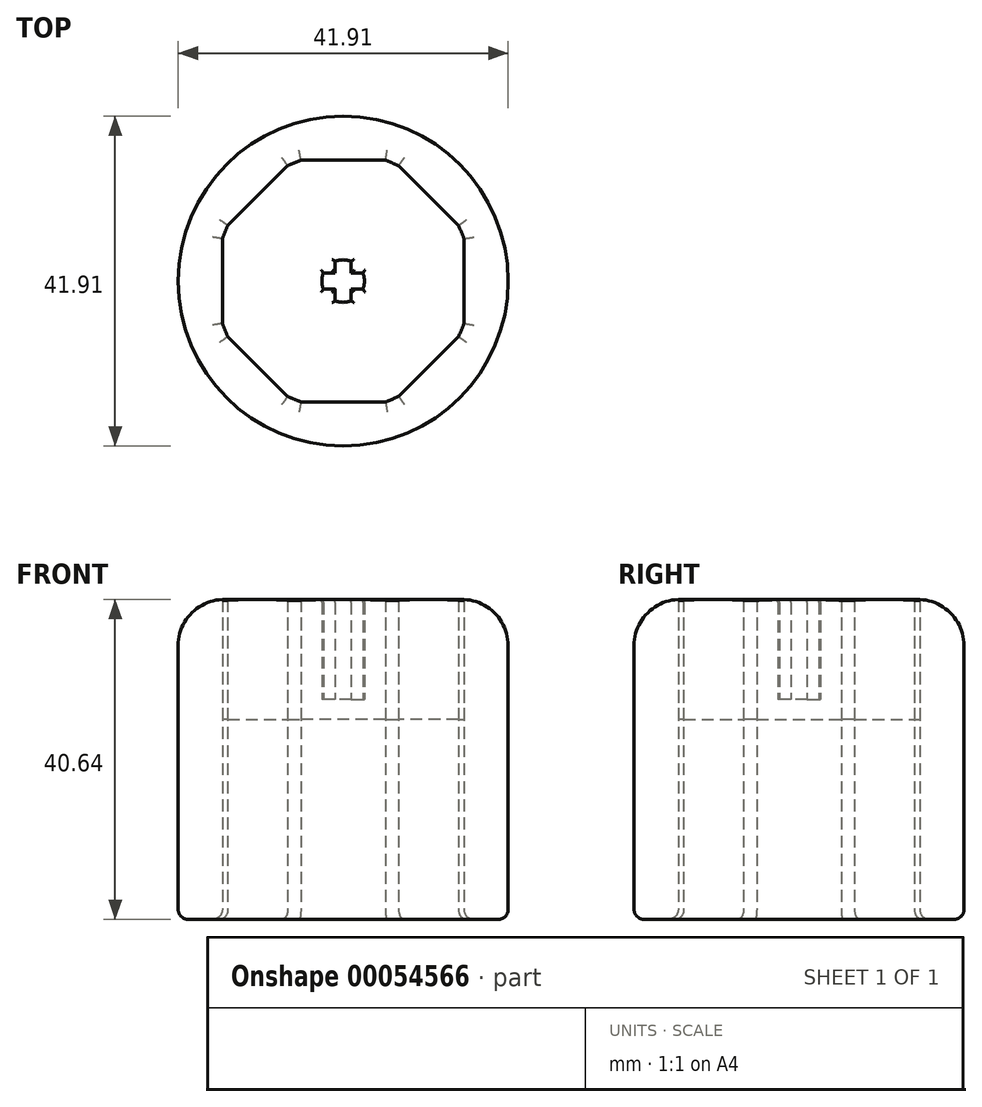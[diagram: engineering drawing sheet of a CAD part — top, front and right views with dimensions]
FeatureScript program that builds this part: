
annotation { "Feature Type Name" : "Feature", "Feature Type Description" : "" }
export const myFeature = defineFeature(function(context is Context, id is Id, definition is map)
    precondition{}
    {
        {
            var Q0;
            Q0=qCreatedBy(makeId("Top.planeOp"),FACE);
            var sketch = newSketch(context, id + "F0", { "sketchPlane" : qUnion([Q0])});
            skLineSegment(sketch, "E0.6.0", {"start": v(-22.54, 38.16) * mm, "end": v(-22.54, 27.4) * mm});
            skLineSegment(sketch, "E0.4.0", {"start": v(-32.51, 17.44) * mm, "end": v(-43.26, 17.44) * mm});
            skLineSegment(sketch, "E0.3.0", {"start": v(-44.93, 18.13) * mm, "end": v(-52.54, 25.73) * mm});
            skLineSegment(sketch, "E0.7.0", {"start": v(-30.84, 47.43) * mm, "end": v(-23.24, 39.83) * mm});
            skLineSegment(sketch, "E0.5.0", {"start": v(-23.24, 25.73) * mm, "end": v(-30.84, 18.13) * mm});
            skLineSegment(sketch, "E0.2.0", {"start": v(-53.23, 27.4) * mm, "end": v(-53.23, 38.16) * mm});
            skLineSegment(sketch, "E0.1.0", {"start": v(-52.54, 39.83) * mm, "end": v(-44.93, 47.43) * mm});
            skLineSegment(sketch, "E1", {"start": v(-43.26, 48.12) * mm, "end": v(-32.51, 48.12) * mm});
            skArc(sketch, "E2.trimOffspring", {"start": v(-32.51, 17.44) * mm, "mid": v(-31.67, 17.76) * mm, "end": v(-30.84, 18.13) * mm});
            skArc(sketch, "E3.trimOffspring", {"start": v(-30.84, 47.43) * mm, "mid": v(-31.67, 47.8) * mm, "end": v(-32.51, 48.12) * mm});
            skArc(sketch, "E4.trimOffspring", {"start": v(-43.26, 48.12) * mm, "mid": v(-44.1, 47.8) * mm, "end": v(-44.93, 47.43) * mm});
            skArc(sketch, "E5", {"start": v(-52.54, 39.83) * mm, "mid": v(-52.9, 39) * mm, "end": v(-53.23, 38.16) * mm});
            skArc(sketch, "E6.trimOffspring", {"start": v(-22.54, 38.16) * mm, "mid": v(-22.87, 39) * mm, "end": v(-23.24, 39.83) * mm});
            skArc(sketch, "E7.trimOffspring", {"start": v(-53.23, 27.4) * mm, "mid": v(-52.9, 26.56) * mm, "end": v(-52.54, 25.73) * mm});
            skArc(sketch, "E8.trimOffspring", {"start": v(-44.93, 18.13) * mm, "mid": v(-44.1, 17.76) * mm, "end": v(-43.26, 17.44) * mm});
            skArc(sketch, "E9.trimOffspring", {"start": v(-23.24, 25.73) * mm, "mid": v(-22.87, 26.56) * mm, "end": v(-22.54, 27.4) * mm});
            skCircle(sketch, "E10", {"center": v(-37.89, 32.78) * mm, "radius": 20.96 * mm});
            skLineSegment(sketch, "E11", {"start": v(-38.9, 31.77) * mm, "end": v(-38.9, 30.28) * mm});
            skLineSegment(sketch, "E12", {"start": v(-36.87, 31.77) * mm, "end": v(-35.38, 31.77) * mm});
            skLineSegment(sketch, "E13", {"start": v(-36.87, 33.8) * mm, "end": v(-36.87, 35.28) * mm});
            skLineSegment(sketch, "E14", {"start": v(-38.9, 31.77) * mm, "end": v(-40.39, 31.77) * mm});
            skArc(sketch, "E15.trimOffspring", {"start": v(-35.38, 31.77) * mm, "mid": v(-35.19, 32.78) * mm, "end": v(-35.38, 33.8) * mm});
            skLineSegment(sketch, "E16", {"start": v(-38.9, 33.8) * mm, "end": v(-40.39, 33.8) * mm});
            skArc(sketch, "E17.trimOffspring", {"start": v(-40.39, 33.8) * mm, "mid": v(-40.59, 32.78) * mm, "end": v(-40.39, 31.77) * mm});
            skLineSegment(sketch, "E18", {"start": v(-38.9, 33.8) * mm, "end": v(-38.9, 35.28) * mm});
            skLineSegment(sketch, "E19", {"start": v(-36.87, 31.77) * mm, "end": v(-36.87, 30.28) * mm});
            skArc(sketch, "E20.trimOffspring", {"start": v(-38.9, 30.28) * mm, "mid": v(-37.89, 30.08) * mm, "end": v(-36.87, 30.28) * mm});
            skArc(sketch, "E21", {"start": v(-36.87, 35.28) * mm, "mid": v(-37.89, 35.48) * mm, "end": v(-38.9, 35.28) * mm});
            skLineSegment(sketch, "E22", {"start": v(-36.87, 33.8) * mm, "end": v(-35.38, 33.8) * mm});
            skCircle(sketch, "E23", {"center": v(-37.89, 32.78) * mm, "radius": 6.35 * mm});
            skSolve(sketch);
        }
        {
            var Q0;
            Q0=makeQuery(id+"F0.imprint","IMPRINT",FACE,{"disambiguationData":[TD([[makeQuery(id+"F0.imprint","IMPRINT",EDGE,{"derivedFrom":sQuery(id+"F0.wireOp",EDGE,"E11")}),1.0]])]});
            extrude(context, id + "F1", {"entities" : qUnion([Q0]), "depth" : 27.94 * mm, "hasSecondDirection" : true, "secondDirectionOppositeDirection" : false, "secondDirectionDepth" : 25.4 * mm});
        }
        {
            var Q0;
            Q0=makeQuery(id+"F0.imprint","IMPRINT",FACE,{"disambiguationData":[TD([[makeQuery(id+"F0.imprint","IMPRINT",EDGE,{"derivedFrom":sQuery(id+"F0.wireOp",EDGE,"E11")}),-1.0]])]});
            extrude(context, id + "F2", {"entities" : qUnion([Q0]), "operationType" : NewBodyOperationType.ADD, "depth" : 40.64 * mm, "hasSecondDirection" : true, "secondDirectionOppositeDirection" : false, "secondDirectionDepth" : 25.4 * mm});
        }
        {
            var Q0;
            Q0=makeQuery(id+"F0.imprint","IMPRINT",FACE,{"disambiguationData":[TD([[makeQuery(id+"F0.imprint","IMPRINT",EDGE,{"derivedFrom":sQuery(id+"F0.wireOp",EDGE,"E0.6.0")}),-1.0]])]});
            extrude(context, id + "F3", {"entities" : qUnion([Q0]), "operationType" : NewBodyOperationType.ADD, "depth" : 40.64 * mm, "hasSecondDirection" : true, "secondDirectionOppositeDirection" : false, "secondDirectionDepth" : 25.4 * mm});
        }
        {
            var Q0;
            Q0=makeQuery(id+"F0.imprint","IMPRINT",FACE,{"disambiguationData":[TD([[makeQuery(id+"F0.imprint","IMPRINT",EDGE,{"derivedFrom":sQuery(id+"F0.wireOp",EDGE,"E0.6.0")}),1.0]])]});
            extrude(context, id + "F4", {"entities" : qUnion([Q0]), "depth" : 40.64 * mm});
        }
        {
            var Q0;
            Q0=makeQuery(id+"F2.opExtrude","CAP_EDGE",EDGE,{"disambiguationData":[OSD([sQuery(id+"F0.wireOp",EDGE,"8cce3f25-2efd-4c49-95cc-eba16443d6be")])],"isStart":false});
            var Q1;
            Q1=makeQuery(id+"F2.opExtrude","CAP_EDGE",EDGE,{"disambiguationData":[OSD([sQuery(id+"F0.wireOp",EDGE,"d85cb93b-5381-4659-b75b-9c5bd339f56e.trimOffspring")])],"isStart":false});
            var Q2;
            Q2=makeQuery(id+"F2.opExtrude","CAP_EDGE",EDGE,{"disambiguationData":[OSD([sQuery(id+"F0.wireOp",EDGE,"1c712a26-7b62-46fb-a9db-95f78db6a6e8")])],"isStart":false});
            var Q3;
            Q3=makeQuery(id+"F2.opExtrude","CAP_EDGE",EDGE,{"disambiguationData":[OSD([sQuery(id+"F0.wireOp",EDGE,"b9b189e9-58f7-485b-9be6-83cfb21979a9")])],"isStart":false});
            var Q4;
            Q4=makeQuery(id+"F2.opExtrude","CAP_EDGE",EDGE,{"disambiguationData":[OSD([sQuery(id+"F0.wireOp",EDGE,"06b7407c-ebd2-401f-a168-bfd0f99af218.trimOffspring")])],"isStart":false});
            var Q5;
            Q5=makeQuery(id+"F2.opExtrude","CAP_EDGE",EDGE,{"disambiguationData":[OSD([sQuery(id+"F0.wireOp",EDGE,"24feb4b3-b69e-498d-8aa6-f2a153c40b04")])],"isStart":false});
            var Q6;
            Q6=makeQuery(id+"F2.opExtrude","CAP_EDGE",EDGE,{"disambiguationData":[OSD([sQuery(id+"F0.wireOp",EDGE,"b4d91fd9-bfef-4f18-a990-5c9c65c2c351.trimOffspring")])],"isStart":false});
            var Q7;
            Q7=makeQuery(id+"F2.opExtrude","CAP_EDGE",EDGE,{"disambiguationData":[OSD([sQuery(id+"F0.wireOp",EDGE,"6bb57907-a155-48d2-a021-7ef5ce16fcda")])],"isStart":false});
            var Q8;
            Q8=makeQuery(id+"F2.opExtrude","CAP_EDGE",EDGE,{"disambiguationData":[OSD([sQuery(id+"F0.wireOp",EDGE,"65d8ba4e-4099-4971-ac6f-0856e3ba22bd")])],"isStart":false});
            var Q9;
            Q9=makeQuery(id+"F2.opExtrude","CAP_EDGE",EDGE,{"disambiguationData":[OSD([sQuery(id+"F0.wireOp",EDGE,"1507f4e8-23c1-4ea5-b1ae-361abdb5c639")])],"isStart":false});
            var Q10;
            Q10=makeQuery(id+"F2.opExtrude","CAP_EDGE",EDGE,{"disambiguationData":[OSD([sQuery(id+"F0.wireOp",EDGE,"df5c5b97-d7ba-45ac-b841-1a60e982e43c")])],"isStart":false});
            var Q11;
            Q11=makeQuery(id+"F2.opExtrude","CAP_EDGE",EDGE,{"disambiguationData":[OSD([sQuery(id+"F0.wireOp",EDGE,"63e4fde5-60d5-43d3-8cb7-058ddb4870cb")])],"isStart":false});
            var Q12;
            Q12=makeQuery(id+"F2.opExtrude","CAP_EDGE",EDGE,{"disambiguationData":[OSD([sQuery(id+"F0.wireOp",EDGE,"E22")])],"isStart":false});
            var Q13;
            Q13=makeQuery(id+"F2.opExtrude","CAP_EDGE",EDGE,{"disambiguationData":[OSD([sQuery(id+"F0.wireOp",EDGE,"E15.trimOffspring")])],"isStart":false});
            var Q14;
            Q14=makeQuery(id+"F2.opExtrude","CAP_EDGE",EDGE,{"disambiguationData":[OSD([sQuery(id+"F0.wireOp",EDGE,"E19")])],"isStart":false});
            var Q15;
            Q15=makeQuery(id+"F2.opExtrude","CAP_EDGE",EDGE,{"disambiguationData":[OSD([sQuery(id+"F0.wireOp",EDGE,"E13")])],"isStart":false});
            var Q16;
            Q16=makeQuery(id+"F2.opExtrude","CAP_EDGE",EDGE,{"disambiguationData":[OSD([sQuery(id+"F0.wireOp",EDGE,"E21")])],"isStart":false});
            var Q17;
            Q17=makeQuery(id+"F2.opExtrude","CAP_EDGE",EDGE,{"disambiguationData":[OSD([sQuery(id+"F0.wireOp",EDGE,"E12")])],"isStart":false});
            var Q18;
            Q18=makeQuery(id+"F2.opExtrude","CAP_EDGE",EDGE,{"disambiguationData":[OSD([sQuery(id+"F0.wireOp",EDGE,"E16")])],"isStart":false});
            var Q19;
            Q19=makeQuery(id+"F2.opExtrude","CAP_EDGE",EDGE,{"disambiguationData":[OSD([sQuery(id+"F0.wireOp",EDGE,"E18")])],"isStart":false});
            var Q20;
            Q20=makeQuery(id+"F2.opExtrude","CAP_EDGE",EDGE,{"disambiguationData":[OSD([sQuery(id+"F0.wireOp",EDGE,"E14")])],"isStart":false});
            var Q21;
            Q21=makeQuery(id+"F2.opExtrude","CAP_EDGE",EDGE,{"disambiguationData":[OSD([sQuery(id+"F0.wireOp",EDGE,"E17.trimOffspring")])],"isStart":false});
            var Q22;
            Q22=makeQuery(id+"F2.opExtrude","CAP_EDGE",EDGE,{"disambiguationData":[OSD([sQuery(id+"F0.wireOp",EDGE,"E11")])],"isStart":false});
            var Q23;
            Q23=makeQuery(id+"F2.opExtrude","CAP_EDGE",EDGE,{"disambiguationData":[OSD([sQuery(id+"F0.wireOp",EDGE,"E20.trimOffspring")])],"isStart":false});
            fillet(context, id + "F5", {"entities" : qUnion([Q0, Q1, Q2, Q3, Q4, Q5, Q6, Q7, Q8, Q9, Q10, Q11, Q12, Q13, Q14, Q15, Q16, Q17, Q18, Q19, Q20, Q21, Q22, Q23]), "radius" : 0.38 * mm, "tangentPropagation" : true, "allowEdgeOverflow" : false});
        }
        {
            var Q0;
            Q0=makeQuery(id+"F4.opExtrude","CAP_EDGE",EDGE,{"disambiguationData":[OSD([sQuery(id+"F0.wireOp",EDGE,"34b97c57-4139-4ba9-9a9e-a1f90fe492f6")])],"isStart":false});
            var Q1;
            Q1=makeQuery(id+"F4.opExtrude","CAP_EDGE",EDGE,{"disambiguationData":[OSD([sQuery(id+"F0.wireOp",EDGE,"E10")])],"isStart":false});
            fillet(context, id + "F6", {"entities" : qUnion([Q0, Q1]), "radius" : 5.84 * mm, "tangentPropagation" : true, "allowEdgeOverflow" : false});
        }
        {
            var Q0;
            Q0=makeQuery(id+"F4.opExtrude","CAP_EDGE",EDGE,{"disambiguationData":[OSD([sQuery(id+"F0.wireOp",EDGE,"34b97c57-4139-4ba9-9a9e-a1f90fe492f6")])],"isStart":true});
            var Q1;
            Q1=makeQuery(id+"F4.opExtrude","CAP_EDGE",EDGE,{"disambiguationData":[OSD([sQuery(id+"F0.wireOp",EDGE,"e68f5cd1-f7fe-44bd-84ca-22998c78a58e.3.0")])],"isStart":true});
            var Q2;
            Q2=makeQuery(id+"F4.opExtrude","CAP_EDGE",EDGE,{"disambiguationData":[OSD([sQuery(id+"F0.wireOp",EDGE,"e68f5cd1-f7fe-44bd-84ca-22998c78a58e.2.0")])],"isStart":true});
            var Q3;
            Q3=makeQuery(id+"F4.opExtrude","CAP_EDGE",EDGE,{"disambiguationData":[OSD([sQuery(id+"F0.wireOp",EDGE,"19dd5a60-77d2-466b-ad95-392809fea93a.trimOffspring")])],"isStart":true});
            var Q4;
            Q4=makeQuery(id+"F4.opExtrude","CAP_EDGE",EDGE,{"disambiguationData":[OSD([sQuery(id+"F0.wireOp",EDGE,"cbcc1692-128e-4c7d-bcf3-f8956db3017d.trimOffspring")])],"isStart":true});
            var Q5;
            Q5=makeQuery(id+"F4.opExtrude","CAP_EDGE",EDGE,{"disambiguationData":[OSD([sQuery(id+"F0.wireOp",EDGE,"e68f5cd1-f7fe-44bd-84ca-22998c78a58e.4.0")])],"isStart":true});
            var Q6;
            Q6=makeQuery(id+"F4.opExtrude","CAP_EDGE",EDGE,{"disambiguationData":[OSD([sQuery(id+"F0.wireOp",EDGE,"9069cb0e-2177-4baf-a3e2-3174a85d6ad9.trimOffspring")])],"isStart":true});
            var Q7;
            Q7=makeQuery(id+"F4.opExtrude","CAP_EDGE",EDGE,{"disambiguationData":[OSD([sQuery(id+"F0.wireOp",EDGE,"e68f5cd1-f7fe-44bd-84ca-22998c78a58e.5.0")])],"isStart":true});
            var Q8;
            Q8=makeQuery(id+"F4.opExtrude","CAP_EDGE",EDGE,{"disambiguationData":[OSD([sQuery(id+"F0.wireOp",EDGE,"e68f5cd1-f7fe-44bd-84ca-22998c78a58e.1.0")])],"isStart":true});
            var Q9;
            Q9=makeQuery(id+"F4.opExtrude","CAP_EDGE",EDGE,{"disambiguationData":[OSD([sQuery(id+"F0.wireOp",EDGE,"f1c67b7e-82c5-4710-8c8e-e395814cc59c")])],"isStart":true});
            var Q10;
            Q10=makeQuery(id+"F4.opExtrude","CAP_EDGE",EDGE,{"disambiguationData":[OSD([sQuery(id+"F0.wireOp",EDGE,"e37a4532-e548-428b-b1e3-5847a7a48128.trimOffspring")])],"isStart":true});
            var Q11;
            Q11=makeQuery(id+"F4.opExtrude","CAP_EDGE",EDGE,{"disambiguationData":[OSD([sQuery(id+"F0.wireOp",EDGE,"de9b58ae-a5a9-4085-9be6-9b22788d534f")])],"isStart":true});
            var Q12;
            Q12=makeQuery(id+"F4.opExtrude","CAP_EDGE",EDGE,{"disambiguationData":[OSD([sQuery(id+"F0.wireOp",EDGE,"52c18542-8fb8-4f89-9851-0ef82118795b.trimOffspring")])],"isStart":true});
            var Q13;
            Q13=makeQuery(id+"F4.opExtrude","CAP_EDGE",EDGE,{"disambiguationData":[OSD([sQuery(id+"F0.wireOp",EDGE,"e68f5cd1-f7fe-44bd-84ca-22998c78a58e.7.0")])],"isStart":true});
            var Q14;
            Q14=makeQuery(id+"F4.opExtrude","CAP_EDGE",EDGE,{"disambiguationData":[OSD([sQuery(id+"F0.wireOp",EDGE,"8ed46637-40c6-47f1-bd96-06ed971209f6.trimOffspring")])],"isStart":true});
            var Q15;
            Q15=makeQuery(id+"F4.opExtrude","CAP_EDGE",EDGE,{"disambiguationData":[OSD([sQuery(id+"F0.wireOp",EDGE,"e68f5cd1-f7fe-44bd-84ca-22998c78a58e.6.0")])],"isStart":true});
            var Q16;
            Q16=makeQuery(id+"F4.opExtrude","CAP_EDGE",EDGE,{"disambiguationData":[OSD([sQuery(id+"F0.wireOp",EDGE,"304d518d-eded-4194-8c4c-5d27241cf2a7.trimOffspring")])],"isStart":true});
            var Q17;
            Q17=makeQuery(id+"F4.opExtrude","CAP_EDGE",EDGE,{"disambiguationData":[OSD([sQuery(id+"F0.wireOp",EDGE,"E10")])],"isStart":true});
            var Q18;
            Q18=makeQuery(id+"F4.opExtrude","CAP_EDGE",EDGE,{"disambiguationData":[OSD([sQuery(id+"F0.wireOp",EDGE,"E0.4.0")])],"isStart":true});
            var Q19;
            Q19=makeQuery(id+"F4.opExtrude","CAP_EDGE",EDGE,{"disambiguationData":[OSD([sQuery(id+"F0.wireOp",EDGE,"E0.3.0")])],"isStart":true});
            var Q20;
            Q20=makeQuery(id+"F4.opExtrude","CAP_EDGE",EDGE,{"disambiguationData":[OSD([sQuery(id+"F0.wireOp",EDGE,"E8.trimOffspring")])],"isStart":true});
            var Q21;
            Q21=makeQuery(id+"F4.opExtrude","CAP_EDGE",EDGE,{"disambiguationData":[OSD([sQuery(id+"F0.wireOp",EDGE,"E2.trimOffspring")])],"isStart":true});
            var Q22;
            Q22=makeQuery(id+"F4.opExtrude","CAP_EDGE",EDGE,{"disambiguationData":[OSD([sQuery(id+"F0.wireOp",EDGE,"E0.5.0")])],"isStart":true});
            var Q23;
            Q23=makeQuery(id+"F4.opExtrude","CAP_EDGE",EDGE,{"disambiguationData":[OSD([sQuery(id+"F0.wireOp",EDGE,"E9.trimOffspring")])],"isStart":true});
            var Q24;
            Q24=makeQuery(id+"F4.opExtrude","CAP_EDGE",EDGE,{"disambiguationData":[OSD([sQuery(id+"F0.wireOp",EDGE,"E0.6.0")])],"isStart":true});
            var Q25;
            Q25=makeQuery(id+"F4.opExtrude","CAP_EDGE",EDGE,{"disambiguationData":[OSD([sQuery(id+"F0.wireOp",EDGE,"E6.trimOffspring")])],"isStart":true});
            var Q26;
            Q26=makeQuery(id+"F4.opExtrude","CAP_EDGE",EDGE,{"disambiguationData":[OSD([sQuery(id+"F0.wireOp",EDGE,"E0.7.0")])],"isStart":true});
            var Q27;
            Q27=makeQuery(id+"F4.opExtrude","CAP_EDGE",EDGE,{"disambiguationData":[OSD([sQuery(id+"F0.wireOp",EDGE,"E7.trimOffspring")])],"isStart":true});
            var Q28;
            Q28=makeQuery(id+"F4.opExtrude","CAP_EDGE",EDGE,{"disambiguationData":[OSD([sQuery(id+"F0.wireOp",EDGE,"E0.2.0")])],"isStart":true});
            var Q29;
            Q29=makeQuery(id+"F4.opExtrude","CAP_EDGE",EDGE,{"disambiguationData":[OSD([sQuery(id+"F0.wireOp",EDGE,"E5")])],"isStart":true});
            var Q30;
            Q30=makeQuery(id+"F4.opExtrude","CAP_EDGE",EDGE,{"disambiguationData":[OSD([sQuery(id+"F0.wireOp",EDGE,"E0.1.0")])],"isStart":true});
            var Q31;
            Q31=makeQuery(id+"F4.opExtrude","CAP_EDGE",EDGE,{"disambiguationData":[OSD([sQuery(id+"F0.wireOp",EDGE,"E4.trimOffspring")])],"isStart":true});
            var Q32;
            Q32=makeQuery(id+"F4.opExtrude","CAP_EDGE",EDGE,{"disambiguationData":[OSD([sQuery(id+"F0.wireOp",EDGE,"E1")])],"isStart":true});
            var Q33;
            Q33=makeQuery(id+"F4.opExtrude","CAP_EDGE",EDGE,{"disambiguationData":[OSD([sQuery(id+"F0.wireOp",EDGE,"E3.trimOffspring")])],"isStart":true});
            fillet(context, id + "F7", {"entities" : qUnion([Q0, Q1, Q2, Q3, Q4, Q5, Q6, Q7, Q8, Q9, Q10, Q11, Q12, Q13, Q14, Q15, Q16, Q17, Q18, Q19, Q20, Q21, Q22, Q23, Q24, Q25, Q26, Q27, Q28, Q29, Q30, Q31, Q32, Q33]), "radius" : 1.27 * mm, "tangentPropagation" : true, "allowEdgeOverflow" : false});
        }
    });
